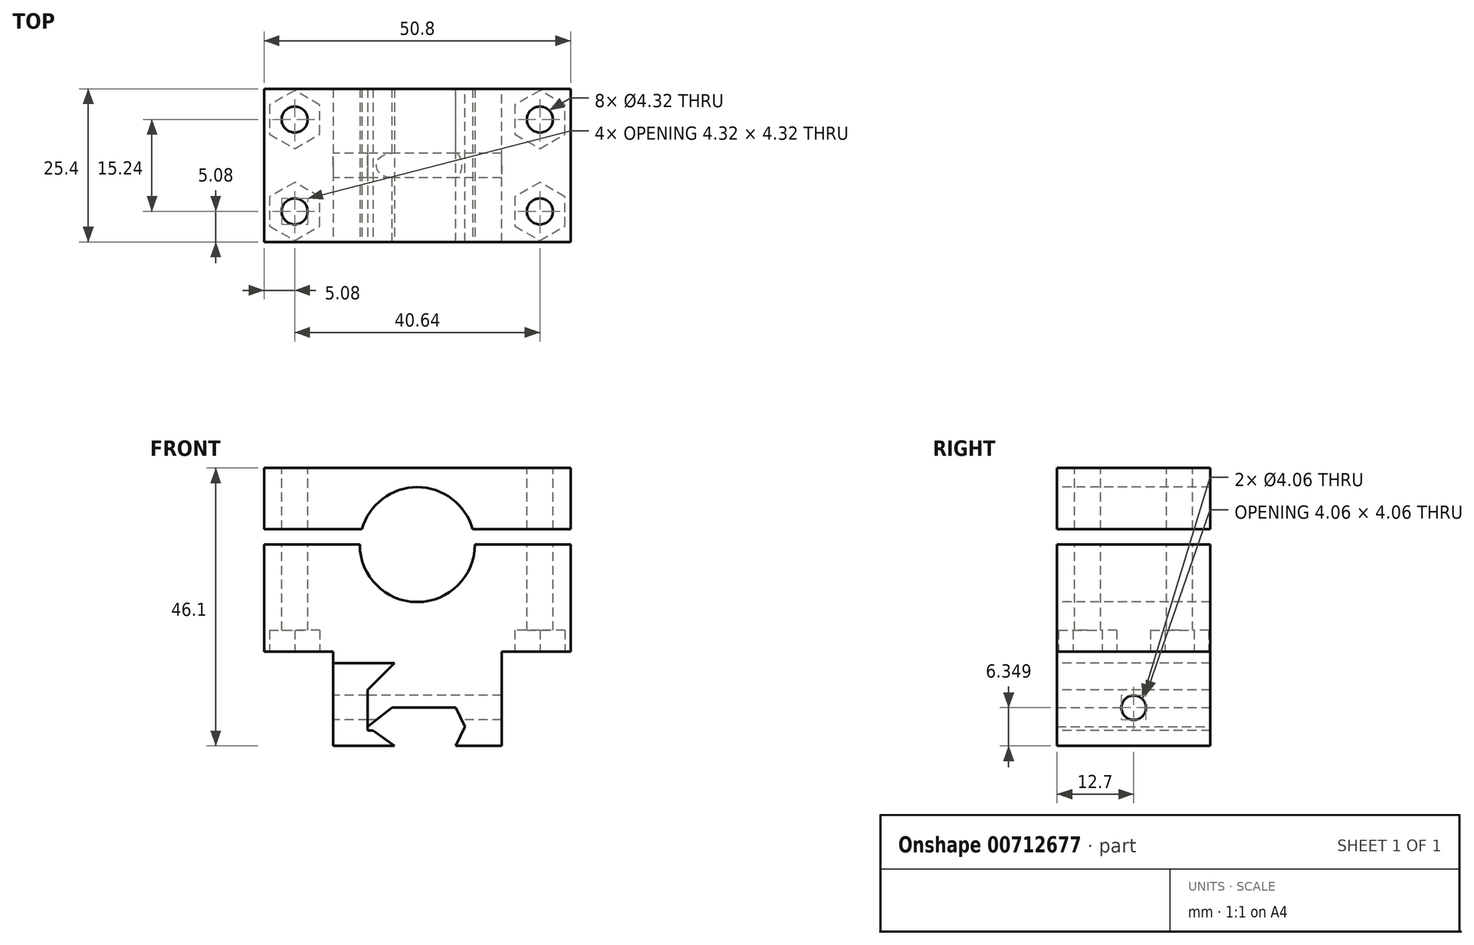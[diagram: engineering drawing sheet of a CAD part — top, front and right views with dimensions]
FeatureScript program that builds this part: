
annotation { "Feature Type Name" : "Feature", "Feature Type Description" : "" }
export const myFeature = defineFeature(function(context is Context, id is Id, definition is map)
    precondition{}
    {
        {
            var Q0;
            Q0=qCreatedBy(makeId("Top.planeOp"),FACE);
            var sketch = newSketch(context, id + "F0", { "sketchPlane" : qUnion([Q0])});
            skLineSegment(sketch, "E0.bottom", {"start": v(-25.4, 12.7) * mm, "end": v(25.4, 12.7) * mm});
            skLineSegment(sketch, "E0.top", {"start": v(-25.4, -12.7) * mm, "end": v(25.4, -12.7) * mm});
            skLineSegment(sketch, "E0.left", {"start": v(-25.4, 12.7) * mm, "end": v(-25.4, -12.7) * mm});
            skLineSegment(sketch, "E0.right", {"start": v(25.4, 12.7) * mm, "end": v(25.4, -12.7) * mm});
            skPoint(sketch, "E0.middle", {"position": v(0, 0) * mm});
            skSolve(sketch);
        }
        {
            var Q0;
            Q0 = qSketchRegion(id + "F0", true);
            extrude(context, id + "F1", {"entities" : qUnion([Q0]), "depth" : 17.78 * mm, "offsetDistance" : 25.4 * mm});
        }
        {
            var Q0;
            Q0=makeQuery(id+"F1.opExtrude","SWEPT_FACE",FACE,{"disambiguationData":[OSD([sQuery(id+"F0.wireOp",EDGE,"E0.top")])]});
            var sketch = newSketch(context, id + "F2", { "sketchPlane" : qUnion([Q0])});
            skCircle(sketch, "E1", {"center": v(0, 17.78) * mm, "radius": 9.53 * mm});
            skSolve(sketch);
        }
        {
            var Q0;
            {var subQ0=sQuery(id+"F0.wireOp",EDGE,"E0.bottom");var subQ1=sQuery(id+"F0.wireOp",EDGE,"E0.top");var subQ2=sQuery(id+"F0.wireOp",EDGE,"E0.left");Q0=makeQuery(id+"F5.boolean.opBoolean","SPLIT",FACE,{"disambiguationData":[TD([makeQuery(id+"F1.opExtrude","SWEPT_FACE",FACE,{"disambiguationData":[OSD([subQ2])]})])],"derivedFrom":makeQuery(id+"F1.opExtrude","CAP_FACE",FACE,{"disambiguationData":[OSD([subQ0,subQ1,subQ2,sQuery(id+"F0.wireOp",EDGE,"E0.right")])],"isStart":false})});}
            var sketch = newSketch(context, id + "F3", { "sketchPlane" : qUnion([Q0])});
            skLineSegment(sketch, "E2.bottom", {"start": v(-25.4, 12.7) * mm, "end": v(25.4, 12.7) * mm});
            skLineSegment(sketch, "E2.top", {"start": v(-25.4, -12.7) * mm, "end": v(25.4, -12.7) * mm});
            skLineSegment(sketch, "E2.left", {"start": v(-25.4, 12.7) * mm, "end": v(-25.4, -12.7) * mm});
            skLineSegment(sketch, "E2.right", {"start": v(25.4, 12.7) * mm, "end": v(25.4, -12.7) * mm});
            skSolve(sketch);
        }
        {
            var Q0;
            Q0 = qSketchRegion(id + "F3", true);
            extrude(context, id + "F4", {"entities" : qUnion([Q0]), "depth" : 12.7 * mm, "offsetDistance" : 25.4 * mm});
        }
        {
            var Q0;
            Q0 = qSketchRegion(id + "F2", true);
            extrude(context, id + "F5", {"entities" : qUnion([Q0]), "operationType" : NewBodyOperationType.REMOVE, "oppositeDirection" : true, "depth" : 76.2 * mm, "offsetDistance" : 25.4 * mm});
        }
        {
            var Q0;
            Q0=makeQuery(id+"F4.opExtrude","SWEPT_FACE",FACE,{"disambiguationData":[OSD([sQuery(id+"F3.wireOp",EDGE,"E2.top")])]});
            var sketch = newSketch(context, id + "F6", { "sketchPlane" : qUnion([Q0])});
            skCircle(sketch, "E3", {"center": v(0, 17.78) * mm, "radius": 9.53 * mm});
            skSolve(sketch);
        }
        {
            var Q0;
            Q0 = qSketchRegion(id + "F6", true);
            extrude(context, id + "F7", {"entities" : qUnion([Q0]), "operationType" : NewBodyOperationType.REMOVE, "oppositeDirection" : true, "depth" : 76.2 * mm, "offsetDistance" : 25.4 * mm});
        }
        {
            var Q0;
            {var subQ0=sQuery(id+"F3.wireOp",EDGE,"E2.bottom");var subQ1=sQuery(id+"F3.wireOp",EDGE,"E2.top");var subQ2=sQuery(id+"F3.wireOp",EDGE,"E2.left");Q0=makeQuery(id+"F7.boolean.opBoolean","SPLIT",FACE,{"disambiguationData":[TD([makeQuery(id+"F4.opExtrude","SWEPT_FACE",FACE,{"disambiguationData":[OSD([subQ2])]})])],"derivedFrom":makeQuery(id+"F4.opExtrude","CAP_FACE",FACE,{"disambiguationData":[OSD([subQ0,subQ1,subQ2,sQuery(id+"F3.wireOp",EDGE,"E2.right")])],"isStart":true})});}
            var sketch = newSketch(context, id + "F8", { "sketchPlane" : qUnion([Q0])});
            skLineSegment(sketch, "E4.bottom", {"start": v(-25.4, 12.7) * mm, "end": v(50.8, 12.7) * mm});
            skLineSegment(sketch, "E4.top", {"start": v(-25.4, -45.7) * mm, "end": v(50.8, -45.7) * mm});
            skLineSegment(sketch, "E4.left", {"start": v(-25.4, 12.7) * mm, "end": v(-25.4, -45.7) * mm});
            skLineSegment(sketch, "E4.right", {"start": v(50.8, 12.7) * mm, "end": v(50.8, -45.7) * mm});
            skSolve(sketch);
        }
        {
            var Q0;
            Q0 = qSketchRegion(id + "F8", true);
            extrude(context, id + "F9", {"entities" : qUnion([Q0]), "operationType" : NewBodyOperationType.REMOVE, "oppositeDirection" : true, "depth" : 2.54 * mm, "offsetDistance" : 25.4 * mm});
        }
        {
            var Q0;
            {var subQ0=sQuery(id+"F0.wireOp",EDGE,"E0.bottom");var subQ1=sQuery(id+"F0.wireOp",EDGE,"E0.top");var subQ2=sQuery(id+"F0.wireOp",EDGE,"E0.left");Q0=makeQuery(id+"F5.boolean.opBoolean","SPLIT",FACE,{"disambiguationData":[TD([makeQuery(id+"F1.opExtrude","SWEPT_FACE",FACE,{"disambiguationData":[OSD([subQ2])]})])],"derivedFrom":makeQuery(id+"F1.opExtrude","CAP_FACE",FACE,{"disambiguationData":[OSD([subQ0,subQ1,subQ2,sQuery(id+"F0.wireOp",EDGE,"E0.right")])],"isStart":false})});}
            var sketch = newSketch(context, id + "F10", { "sketchPlane" : qUnion([Q0])});
            skCircle(sketch, "E5", {"center": v(-20.32, -7.62) * mm, "radius": 2.16 * mm});
            skCircle(sketch, "E6", {"center": v(-20.32, 7.62) * mm, "radius": 2.16 * mm});
            skSolve(sketch);
        }
        {
            var Q0;
            Q0 = qSketchRegion(id + "F10", true);
            extrude(context, id + "F11", {"entities" : qUnion([Q0]), "operationType" : NewBodyOperationType.REMOVE, "endBound" : BoundingType.THROUGH_ALL, "oppositeDirection" : true, "depth" : 27.18 * mm, "offsetDistance" : 25.4 * mm, "hasSecondDirection" : true, "secondDirectionOppositeDirection" : false, "secondDirectionDepth" : 25.4 * mm});
        }
        {
            var Q0;
            {var subQ0=sQuery(id+"F0.wireOp",EDGE,"E0.bottom");var subQ1=sQuery(id+"F0.wireOp",EDGE,"E0.right");var subQ2=sQuery(id+"F0.wireOp",EDGE,"E0.top");Q0=makeQuery(id+"F5.boolean.opBoolean","SPLIT",FACE,{"disambiguationData":[TD([makeQuery(id+"F1.opExtrude","SWEPT_FACE",FACE,{"disambiguationData":[OSD([subQ1])]})])],"derivedFrom":makeQuery(id+"F1.opExtrude","CAP_FACE",FACE,{"disambiguationData":[OSD([subQ0,subQ2,sQuery(id+"F0.wireOp",EDGE,"E0.left"),subQ1])],"isStart":false})});}
            var sketch = newSketch(context, id + "F12", { "sketchPlane" : qUnion([Q0])});
            skCircle(sketch, "E7", {"center": v(20.32, -7.62) * mm, "radius": 2.16 * mm});
            skCircle(sketch, "E8", {"center": v(20.32, 7.62) * mm, "radius": 2.16 * mm});
            skSolve(sketch);
        }
        {
            var Q0;
            Q0 = qSketchRegion(id + "F12", true);
            extrude(context, id + "F13", {"entities" : qUnion([Q0]), "operationType" : NewBodyOperationType.REMOVE, "oppositeDirection" : true, "depth" : 25.4 * mm, "offsetDistance" : 25.4 * mm, "hasSecondDirection" : true, "secondDirectionOppositeDirection" : false, "secondDirectionDepth" : 25.4 * mm});
        }
        {
            var Q0;
            Q0=makeQuery(id+"F1.opExtrude","CAP_FACE",FACE,{"disambiguationData":[OSD([sQuery(id+"F0.wireOp",EDGE,"E0.bottom"),sQuery(id+"F0.wireOp",EDGE,"E0.top"),sQuery(id+"F0.wireOp",EDGE,"E0.left"),sQuery(id+"F0.wireOp",EDGE,"E0.right")])],"isStart":true});
            var sketch = newSketch(context, id + "F14", { "sketchPlane" : qUnion([Q0])});
            skCircle(sketch, "E9.cCircle", {"center": v(-20.32, 7.62) * mm, "radius": 4.83 * mm, "construction": true});
            skLineSegment(sketch, "E9.0", {"start": v(-16.14, 5.2) * mm, "end": v(-20.32, 2.8) * mm});
            skLineSegment(sketch, "E9.1", {"start": v(-20.32, 2.8) * mm, "end": v(-24.5, 5.2) * mm});
            skLineSegment(sketch, "E9.2", {"start": v(-24.5, 5.2) * mm, "end": v(-24.5, 10.03) * mm});
            skLineSegment(sketch, "E9.3", {"start": v(-24.5, 10.03) * mm, "end": v(-20.32, 12.45) * mm});
            skLineSegment(sketch, "E9.4", {"start": v(-20.32, 12.45) * mm, "end": v(-16.14, 10.03) * mm});
            skLineSegment(sketch, "E9.5", {"start": v(-16.14, 10.03) * mm, "end": v(-16.14, 5.2) * mm});
            skCircle(sketch, "E10.cCircle", {"center": v(-20.32, -7.62) * mm, "radius": 4.83 * mm, "construction": true});
            skLineSegment(sketch, "E10.0", {"start": v(-20.32, -2.8) * mm, "end": v(-16.14, -5.2) * mm});
            skLineSegment(sketch, "E10.1", {"start": v(-16.14, -5.2) * mm, "end": v(-16.14, -10.03) * mm});
            skLineSegment(sketch, "E10.2", {"start": v(-16.14, -10.03) * mm, "end": v(-20.32, -12.45) * mm});
            skLineSegment(sketch, "E10.3", {"start": v(-20.32, -12.45) * mm, "end": v(-24.5, -10.03) * mm});
            skLineSegment(sketch, "E10.4", {"start": v(-24.5, -10.03) * mm, "end": v(-24.5, -5.2) * mm});
            skLineSegment(sketch, "E10.5", {"start": v(-24.5, -5.2) * mm, "end": v(-20.32, -2.8) * mm});
            skCircle(sketch, "E11.cCircle", {"center": v(20.32, 7.62) * mm, "radius": 4.83 * mm, "construction": true});
            skLineSegment(sketch, "E11.0", {"start": v(20.32, 2.8) * mm, "end": v(16.14, 5.2) * mm});
            skLineSegment(sketch, "E11.1", {"start": v(16.14, 5.2) * mm, "end": v(16.14, 10.03) * mm});
            skLineSegment(sketch, "E11.2", {"start": v(16.14, 10.03) * mm, "end": v(20.32, 12.45) * mm});
            skLineSegment(sketch, "E11.3", {"start": v(20.32, 12.45) * mm, "end": v(24.5, 10.03) * mm});
            skLineSegment(sketch, "E11.4", {"start": v(24.5, 10.03) * mm, "end": v(24.5, 5.2) * mm});
            skLineSegment(sketch, "E11.5", {"start": v(24.5, 5.2) * mm, "end": v(20.32, 2.8) * mm});
            skCircle(sketch, "E12.cCircle", {"center": v(20.32, -7.62) * mm, "radius": 4.83 * mm, "construction": true});
            skLineSegment(sketch, "E12.0", {"start": v(24.5, -5.2) * mm, "end": v(24.5, -10.03) * mm});
            skLineSegment(sketch, "E12.1", {"start": v(24.5, -10.03) * mm, "end": v(20.32, -12.45) * mm});
            skLineSegment(sketch, "E12.2", {"start": v(20.32, -12.45) * mm, "end": v(16.14, -10.03) * mm});
            skLineSegment(sketch, "E12.3", {"start": v(16.14, -10.03) * mm, "end": v(16.14, -5.2) * mm});
            skLineSegment(sketch, "E12.4", {"start": v(16.14, -5.2) * mm, "end": v(20.32, -2.8) * mm});
            skLineSegment(sketch, "E12.5", {"start": v(20.32, -2.8) * mm, "end": v(24.5, -5.2) * mm});
            skSolve(sketch);
        }
        {
            var Q0;
            Q0 = qSketchRegion(id + "F14", true);
            extrude(context, id + "F15", {"entities" : qUnion([Q0]), "operationType" : NewBodyOperationType.REMOVE, "oppositeDirection" : true, "depth" : 3.56 * mm, "offsetDistance" : 25.4 * mm});
        }
        {
            var Q0;
            Q0=makeQuery(id+"F1.opExtrude","CAP_FACE",FACE,{"disambiguationData":[OSD([sQuery(id+"F0.wireOp",EDGE,"E0.bottom"),sQuery(id+"F0.wireOp",EDGE,"E0.top"),sQuery(id+"F0.wireOp",EDGE,"E0.left"),sQuery(id+"F0.wireOp",EDGE,"E0.right")])],"isStart":true});
            var sketch = newSketch(context, id + "F16", { "sketchPlane" : qUnion([Q0])});
            skLineSegment(sketch, "E13.bottom", {"start": v(-13.97, 12.7) * mm, "end": v(13.97, 12.7) * mm});
            skLineSegment(sketch, "E13.top", {"start": v(-13.97, -12.7) * mm, "end": v(13.97, -12.7) * mm});
            skLineSegment(sketch, "E13.left", {"start": v(-13.97, 12.7) * mm, "end": v(-13.97, -12.7) * mm});
            skLineSegment(sketch, "E13.right", {"start": v(13.97, 12.7) * mm, "end": v(13.97, -12.7) * mm});
            skLineSegment(sketch, "E14", {"start": v(-25.4, 0) * mm, "end": v(25.4, 0) * mm});
            skSolve(sketch);
        }
        {
            var Q0;
            {var subQ2=sQuery(id+"F16.wireOp",EDGE,"E13.bottom");Q0=makeQuery(id+"F16.imprint","IMPRINT",FACE,{"disambiguationData":[TD([[makeQuery(id+"F16.imprint","IMPRINT",EDGE,{"derivedFrom":subQ2}),-1.0]])]});}
            var Q1;
            {var subQ4=sQuery(id+"F16.wireOp",EDGE,"E13.top");Q1=makeQuery(id+"F16.imprint","IMPRINT",FACE,{"disambiguationData":[TD([[makeQuery(id+"F16.imprint","IMPRINT",EDGE,{"derivedFrom":subQ4}),1.0]])]});}
            extrude(context, id + "F17", {"entities" : qUnion([Q0, Q1]), "operationType" : NewBodyOperationType.ADD, "depth" : 1.9 * mm, "offsetDistance" : 25.4 * mm});
        }
        {
            var Q0;
            Q0=makeQuery(id+"F17.opExtrude","CAP_FACE",FACE,{"disambiguationData":[OSD([sQuery(id+"F14.wireOp",EDGE,"E9.0"),sQuery(id+"F14.wireOp",EDGE,"E9.4"),sQuery(id+"F14.wireOp",EDGE,"E9.5"),sQuery(id+"F14.wireOp",EDGE,"E10.0"),sQuery(id+"F14.wireOp",EDGE,"E10.1"),sQuery(id+"F14.wireOp",EDGE,"E10.2"),sQuery(id+"F14.wireOp",EDGE,"E11.0"),sQuery(id+"F14.wireOp",EDGE,"E11.1"),sQuery(id+"F14.wireOp",EDGE,"E11.2"),sQuery(id+"F14.wireOp",EDGE,"E12.2"),sQuery(id+"F14.wireOp",EDGE,"E12.3"),sQuery(id+"F14.wireOp",EDGE,"E12.4"),sQuery(id+"F16.wireOp",EDGE,"E13.bottom"),sQuery(id+"F16.wireOp",EDGE,"E13.top"),sQuery(id+"F16.wireOp",EDGE,"E13.left"),sQuery(id+"F16.wireOp",EDGE,"E13.right")])],"isStart":false});
            var sketch = newSketch(context, id + "F18", { "sketchPlane" : qUnion([Q0])});
            skLineSegment(sketch, "E15.bottom", {"start": v(13.97, -12.7) * mm, "end": v(-8.26, -12.7) * mm});
            skLineSegment(sketch, "E15.top", {"start": v(13.97, 12.7) * mm, "end": v(-8.26, 12.7) * mm});
            skLineSegment(sketch, "E15.left", {"start": v(13.97, -12.7) * mm, "end": v(13.97, 12.7) * mm});
            skLineSegment(sketch, "E15.right", {"start": v(-8.26, -12.7) * mm, "end": v(-8.26, 12.7) * mm});
            skSolve(sketch);
        }
        {
            var Q0;
            Q0 = qSketchRegion(id + "F18", true);
            extrude(context, id + "F19", {"entities" : qUnion([Q0]), "operationType" : NewBodyOperationType.ADD, "depth" : 7.37 * mm, "offsetDistance" : 25.4 * mm});
        }
        {
            var Q0;
            Q0=makeQuery(id+"F19.opExtrude","SWEPT_FACE",FACE,{"disambiguationData":[OSD([sQuery(id+"F18.wireOp",EDGE,"E15.right")])]});
            var sketch = newSketch(context, id + "F20", { "sketchPlane" : qUnion([Q0])});
            skCircle(sketch, "E16", {"center": v(0, -9.27) * mm, "radius": 2.03 * mm});
            skSolve(sketch);
        }
        {
            var Q0;
            Q0=makeQuery(id+"F19.boolean.opBoolean","MERGE",FACE,{"derivedFrom":[makeQuery(id+"F17.boolean.opBoolean","MERGE",FACE,{"derivedFrom":[makeQuery(id+"F1.opExtrude","SWEPT_FACE",FACE,{"disambiguationData":[OSD([sQuery(id+"F0.wireOp",EDGE,"E0.bottom")])]}),makeQuery(id+"F17.opExtrude","SWEPT_FACE",FACE,{"disambiguationData":[OSD([sQuery(id+"F16.wireOp",EDGE,"E13.top")])]})]}),makeQuery(id+"F19.opExtrude","SWEPT_FACE",FACE,{"disambiguationData":[OSD([sQuery(id+"F18.wireOp",EDGE,"E15.bottom")])]})]});
            var sketch = newSketch(context, id + "F21", { "sketchPlane" : qUnion([Q0])});
            skLineSegment(sketch, "E17", {"start": v(8.26, -1.9) * mm, "end": v(3.81, -1.9) * mm});
            skLineSegment(sketch, "E18", {"start": v(3.81, -1.9) * mm, "end": v(8.26, -6.35) * mm});
            skSolve(sketch);
        }
        {
            var Q0;
            {var subQ0=sQuery(id+"F21.wireOp",EDGE,"E17");Q0=makeQuery(id+"F21.imprint","IMPRINT",FACE,{"disambiguationData":[TD([[makeQuery(id+"F21.imprint","IMPRINT",EDGE,{"derivedFrom":subQ0}),1.0]])]});}
            extrude(context, id + "F22", {"entities" : qUnion([Q0]), "operationType" : NewBodyOperationType.REMOVE, "oppositeDirection" : true, "depth" : 50.8 * mm, "offsetDistance" : 25.4 * mm});
        }
        {
            var Q0;
            {var subQ2=sQuery(id+"F18.wireOp",EDGE,"E15.top");var subQ4=sQuery(id+"F0.wireOp",EDGE,"E0.top");var subQ5=sQuery(id+"F18.wireOp",EDGE,"E15.left");var subQ6=sQuery(id+"F18.wireOp",EDGE,"E15.right");Q0=makeQuery(id+"F29.boolean.opBoolean","SPLIT",FACE,{"disambiguationData":[TD([makeQuery(id+"F1.opExtrude","SWEPT_FACE",FACE,{"disambiguationData":[OSD([subQ4])]})])],"derivedFrom":makeQuery(id+"F19.opExtrude","CAP_FACE",FACE,{"disambiguationData":[OSD([sQuery(id+"F18.wireOp",EDGE,"E15.bottom"),subQ2,subQ5,subQ6])],"isStart":false})});}
            var sketch = newSketch(context, id + "F23", { "sketchPlane" : qUnion([Q0])});
            skLineSegment(sketch, "E19.bottom", {"start": v(-8.26, 12.7) * mm, "end": v(13.97, 12.7) * mm});
            skLineSegment(sketch, "E19.top", {"start": v(-8.26, -12.7) * mm, "end": v(13.97, -12.7) * mm});
            skLineSegment(sketch, "E19.left", {"start": v(-8.26, 12.7) * mm, "end": v(-8.26, -12.7) * mm});
            skLineSegment(sketch, "E19.right", {"start": v(13.97, 12.7) * mm, "end": v(13.97, -12.7) * mm});
            skSolve(sketch);
        }
        {
            var Q0;
            Q0 = qSketchRegion(id + "F23", true);
            extrude(context, id + "F24", {"entities" : qUnion([Q0]), "operationType" : NewBodyOperationType.ADD, "depth" : 6.35 * mm, "offsetDistance" : 25.4 * mm});
        }
        {
            var Q0;
            Q0=makeQuery(id+"F24.boolean.opBoolean","MERGE",FACE,{"derivedFrom":[makeQuery(id+"F19.boolean.opBoolean","MERGE",FACE,{"derivedFrom":[makeQuery(id+"F17.boolean.opBoolean","MERGE",FACE,{"derivedFrom":[makeQuery(id+"F1.opExtrude","SWEPT_FACE",FACE,{"disambiguationData":[OSD([sQuery(id+"F0.wireOp",EDGE,"E0.bottom")])]}),makeQuery(id+"F17.opExtrude","SWEPT_FACE",FACE,{"disambiguationData":[OSD([sQuery(id+"F16.wireOp",EDGE,"E13.top")])]})]}),makeQuery(id+"F19.opExtrude","SWEPT_FACE",FACE,{"disambiguationData":[OSD([sQuery(id+"F18.wireOp",EDGE,"E15.bottom")])]})]}),makeQuery(id+"F24.opExtrude","SWEPT_FACE",FACE,{"disambiguationData":[OSD([sQuery(id+"F23.wireOp",EDGE,"E19.top")])]})]});
            var sketch = newSketch(context, id + "F25", { "sketchPlane" : qUnion([Q0])});
            skLineSegment(sketch, "E20", {"start": v(-13.97, -9.27) * mm, "end": v(8.26, -9.27) * mm});
            skLineSegment(sketch, "E21", {"start": v(-7.87, -15.62) * mm, "end": v(-7.87, -12.45) * mm});
            skLineSegment(sketch, "E22", {"start": v(-7.87, -12.45) * mm, "end": v(-13.97, -12.45) * mm});
            skLineSegment(sketch, "E23", {"start": v(-13.97, -15.62) * mm, "end": v(-6.35, -15.62) * mm});
            skLineSegment(sketch, "E24", {"start": v(-7.87, -12.45) * mm, "end": v(-6.35, -15.62) * mm});
            skLineSegment(sketch, "E25", {"start": v(-7.87, -12.45) * mm, "end": v(-6.35, -9.27) * mm});
            skLineSegment(sketch, "E26", {"start": v(8.26, -9.27) * mm, "end": v(4.2, -9.27) * mm});
            skLineSegment(sketch, "E27", {"start": v(4.2, -9.27) * mm, "end": v(8.26, -12.45) * mm});
            skSolve(sketch);
        }
        {
            var Q0;
            {var subQ5=sQuery(id+"F25.wireOp",EDGE,"E24");Q0=makeQuery(id+"F25.imprint","IMPRINT",FACE,{"disambiguationData":[TD([[makeQuery(id+"F25.imprint","IMPRINT",EDGE,{"derivedFrom":subQ5}),1.0]])]});}
            extrude(context, id + "F26", {"entities" : qUnion([Q0]), "operationType" : NewBodyOperationType.REMOVE, "oppositeDirection" : true, "depth" : 50.8 * mm, "offsetDistance" : 25.4 * mm});
        }
        {
            var Q0;
            Q0=makeQuery(id+"F24.boolean.opBoolean","MERGE",FACE,{"derivedFrom":[makeQuery(id+"F19.boolean.opBoolean","MERGE",FACE,{"derivedFrom":[makeQuery(id+"F17.boolean.opBoolean","MERGE",FACE,{"derivedFrom":[makeQuery(id+"F1.opExtrude","SWEPT_FACE",FACE,{"disambiguationData":[OSD([sQuery(id+"F0.wireOp",EDGE,"E0.top")])]}),makeQuery(id+"F17.opExtrude","SWEPT_FACE",FACE,{"disambiguationData":[OSD([sQuery(id+"F16.wireOp",EDGE,"E13.bottom")])]})]}),makeQuery(id+"F19.opExtrude","SWEPT_FACE",FACE,{"disambiguationData":[OSD([sQuery(id+"F18.wireOp",EDGE,"E15.top")])]})]}),makeQuery(id+"F24.opExtrude","SWEPT_FACE",FACE,{"disambiguationData":[OSD([sQuery(id+"F23.wireOp",EDGE,"E19.bottom")])]})]});
            var sketch = newSketch(context, id + "F27", { "sketchPlane" : qUnion([Q0])});
            skLineSegment(sketch, "E28", {"start": v(-13.97, -1.9) * mm, "end": v(-3.81, -1.9) * mm});
            skLineSegment(sketch, "E29", {"start": v(-3.81, -1.9) * mm, "end": v(-8.26, -6.35) * mm});
            skLineSegment(sketch, "E30", {"start": v(-8.26, -6.35) * mm, "end": v(-8.26, -12.45) * mm});
            skLineSegment(sketch, "E31", {"start": v(-8.26, -12.45) * mm, "end": v(-3.81, -15.62) * mm});
            skLineSegment(sketch, "E32", {"start": v(-3.81, -15.62) * mm, "end": v(-13.97, -15.62) * mm});
            skLineSegment(sketch, "E33", {"start": v(-13.97, -15.62) * mm, "end": v(-13.97, -1.9) * mm});
            skLineSegment(sketch, "E34", {"start": v(6.35, -15.62) * mm, "end": v(-13.97, -15.62) * mm});
            skLineSegment(sketch, "E35", {"start": v(-13.97, -13.08) * mm, "end": v(-7.37, -13.08) * mm});
            skLineSegment(sketch, "E36", {"start": v(-8.26, -12.45) * mm, "end": v(-8.26, -13.08) * mm});
            skSolve(sketch);
        }
        {
            var Q0;
            {var subQ1=sQuery(id+"F27.wireOp",EDGE,"E28");Q0=makeQuery(id+"F27.imprint","IMPRINT",FACE,{"disambiguationData":[TD([[makeQuery(id+"F27.imprint","IMPRINT",EDGE,{"derivedFrom":subQ1}),-1.0]])]});}
            var Q1;
            {var subQ0=sQuery(id+"F27.wireOp",EDGE,"E34");var subQ1=sQuery(id+"F27.wireOp",EDGE,"E31");var subQ2=makeQuery(id+"F27.imprint","INTERSECT",VERTEX,{"derivedFrom":[subQ1,subQ0]});Q1=makeQuery(id+"F27.imprint","IMPRINT",FACE,{"disambiguationData":[TD([[makeQuery(id+"F27.imprint","IMPRINT",EDGE,{"disambiguationData":[TD([[subQ2,1.0]])],"derivedFrom":subQ1}),-1.0]])]});}
            extrude(context, id + "F28", {"entities" : qUnion([Q0, Q1]), "oppositeDirection" : true, "depth" : 25.4 * mm, "offsetDistance" : 25.4 * mm});
        }
        {
            var Q0;
            Q0 = qSketchRegion(id + "F20", true);
            extrude(context, id + "F29", {"entities" : qUnion([Q0]), "operationType" : NewBodyOperationType.REMOVE, "oppositeDirection" : true, "depth" : 50.8 * mm, "offsetDistance" : 25.4 * mm, "hasSecondDirection" : true, "secondDirectionOppositeDirection" : false, "secondDirectionDepth" : 25.4 * mm});
        }
    });
